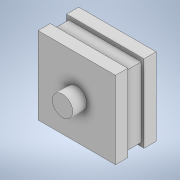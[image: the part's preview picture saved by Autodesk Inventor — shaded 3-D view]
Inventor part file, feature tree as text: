
AUTODESK INVENTOR PART (.ipt)
format: ipt  version: 2022 (Build 260153000, 153)  size: 119,808 bytes
history: native  units: mm
features: extrude x4, sketch x4
ambient origin geometry x8: Origin, YZ Plane, XZ Plane, XY Plane, X Axis, Y Axis, Z Axis, Center Point
bodies: Solid1 (feature_tree)
feature tree (8):
  extrude  "Extrusion1"  Depth=38.1mm
  extrude  "Extrusion2"  Depth=8.0mm TaperAngle=0.0deg
  extrude  "Extrusion3"  Depth=10.0mm
  extrude  "Extrusion4"  Depth=7.0mm
  sketch  "Sketch1"  dims[d0=38.1mm d1=38.1mm]
  sketch  "Sketch2"  dims[d2=6.0mm d3=0.0mm d4=8.0mm d5=0.0mm]
  sketch  "Sketch3"  dims[d6=6.0mm d7=0.0mm d8=10.0mm]
  sketch  "Sketch4"  dims[d9=19.05mm d10=19.05mm d11=7.0mm d12=0.0mm]
